annotation { "Feature Type Name" : "Feature", "Feature Type Description" : "" }
export const myFeature = defineFeature(function(context is Context, id is Id, definition is map)
    precondition{}
    {
        {
            var Q0;
            Q0=qCreatedBy(makeId("Top.planeOp"),FACE);
            var sketch = newSketch(context, id + "F0", { "sketchPlane" : qUnion([Q0])});
            skCircle(sketch, "E0", {"center": v(0, 0) * mm, "radius": 37.5 * mm});
            skSolve(sketch);
        }
        {
            var Q0;
            Q0 = qSketchRegion(id + "F0", true);
            extrude(context, id + "F1", {"entities" : qUnion([Q0]), "depth" : 6 * mm, "offsetDistance" : 25 * mm});
        }
        {
            var Q0;
            Q0=makeQuery(id+"F1.opExtrude","CAP_FACE",FACE,{"disambiguationData":[OSD([sQuery(id+"F0.wireOp",EDGE,"E0")])],"isStart":false});
            var sketch = newSketch(context, id + "F2", { "sketchPlane" : qUnion([Q0])});
            skCircle(sketch, "E1", {"center": v(0, 0) * mm, "radius": 36 * mm});
            skCircle(sketch, "E2.0", {"center": v(0, 0) * mm, "radius": 37.5 * mm});
            skSolve(sketch);
        }
        {
            var Q0;
            Q0 = qSketchRegion(id + "F2", true);
            extrude(context, id + "F3", {"entities" : qUnion([Q0]), "operationType" : NewBodyOperationType.ADD, "depth" : 12 * mm, "offsetDistance" : 25 * mm});
        }
        {
            var Q0;
            Q0=makeQuery(id+"F3.opExtrude","CAP_FACE",FACE,{"disambiguationData":[OSD([sQuery(id+"F2.wireOp",EDGE,"E1"),sQuery(id+"F2.wireOp",EDGE,"E2.0")])],"isStart":false});
            var sketch = newSketch(context, id + "F4", { "sketchPlane" : qUnion([Q0])});
            skArc(sketch, "E3", {"start": v(1.95, -37.45) * mm, "mid": v(2.76, -38.15) * mm, "end": v(3.45, -37.34) * mm});
            skArc(sketch, "E4.0", {"start": v(1.95, -37.45) * mm, "mid": v(2.7, -37.4) * mm, "end": v(3.45, -37.34) * mm});
            skSolve(sketch);
        }
        {
            var Q0;
            Q0=makeQuery(id+"F1.opExtrude","CAP_FACE",FACE,{"disambiguationData":[OSD([sQuery(id+"F0.wireOp",EDGE,"E0")])],"isStart":false});
            var sketch = newSketch(context, id + "F5", { "sketchPlane" : qUnion([Q0])});
            skCircle(sketch, "E5", {"center": v(0, 0) * mm, "radius": 32.75 * mm});
            skCircle(sketch, "E6", {"center": v(0, 0) * mm, "radius": 29.75 * mm});
            skSolve(sketch);
        }
        {
            var Q0;
            Q0 = qSketchRegion(id + "F5", true);
            extrude(context, id + "F6", {"entities" : qUnion([Q0]), "operationType" : NewBodyOperationType.ADD, "depth" : 10 * mm, "offsetDistance" : 25 * mm});
        }
        {
            var Q0;
            Q0=makeQuery(id+"F1.opExtrude","CAP_EDGE",EDGE,{"disambiguationData":[OSD([sQuery(id+"F0.wireOp",EDGE,"E0")])],"isStart":true});
            fillet(context, id + "F7", {"entities" : qUnion([Q0]), "radius" : 5 * mm, "tangentPropagation" : true, "allowEdgeOverflow" : false});
        }
        {
            var Q0;
            Q0=makeQuery(id+"F1.opExtrude","CAP_FACE",FACE,{"disambiguationData":[OSD([sQuery(id+"F0.wireOp",EDGE,"E0")])],"isStart":true});
            var sketch = newSketch(context, id + "F8", { "sketchPlane" : qUnion([Q0])});
            skText(sketch, "E7", { "text": "EXIN LIGHT", "fontName": "OpenSans-Bold.ttf"});
            const initialGuessF8  = {"E7": [-0.03112, -0.00426, 1, 0, 0.008]};
            skSetInitialGuess(sketch, initialGuessF8);
            skSolve(sketch);
        }
        {
            var Q0;
            Q0 = qSketchRegion(id + "F8", true);
            extrude(context, id + "F9", {"entities" : qUnion([Q0]), "operationType" : NewBodyOperationType.REMOVE, "oppositeDirection" : true, "depth" : 1 * mm, "offsetDistance" : 25 * mm});
        }
        {
            var Q0;
            Q0=makeQuery(id+"F1.opExtrude","CAP_FACE",FACE,{"disambiguationData":[OSD([sQuery(id+"F0.wireOp",EDGE,"E0")])],"isStart":true});
            chamfer(context, id + "F10", {"entities" : qUnion([Q0]), "width" : .4 * mm, "tangentPropagation" : true});
        }
        {
            var Q0;
            Q0=makeQuery(id+"F10.opChamfer","SPLIT",FACE,{"disambiguationData":[OD(1.0)],"derivedFrom":makeQuery(id+"F1.opExtrude","CAP_FACE",FACE,{"disambiguationData":[OSD([sQuery(id+"F0.wireOp",EDGE,"E0")])],"isStart":true})});
            var sketch = newSketch(context, id + "F11", { "sketchPlane" : qUnion([Q0])});
            skLineSegment(sketch, "E8.bottom", {"start": v(19.2, -26.22) * mm, "end": v(-19.2, -26.22) * mm});
            skLineSegment(sketch, "E8.top", {"start": v(14.23, -29.22) * mm, "end": v(-14.23, -29.22) * mm});
            skLineSegment(sketch, "E9.0.1.0", {"start": v(25.52, -20.12) * mm, "end": v(-25.52, -20.12) * mm});
            skLineSegment(sketch, "E9.0.1.1", {"start": v(22.84, -23.12) * mm, "end": v(-22.84, -23.12) * mm});
            skLineSegment(sketch, "E9.0.2.0", {"start": v(29.32, -14.02) * mm, "end": v(-29.32, -14.02) * mm});
            skLineSegment(sketch, "E9.0.2.1", {"start": v(27.69, -17.02) * mm, "end": v(-27.69, -17.02) * mm});
            skLineSegment(sketch, "E9.0.3.0", {"start": v(31.52, -7.92) * mm, "end": v(-31.52, -7.92) * mm});
            skLineSegment(sketch, "E9.0.3.1", {"start": v(30.61, -10.92) * mm, "end": v(-30.61, -10.92) * mm});
            skLineSegment(sketch, "E9.0.6.0", {"start": v(30.8, 10.38) * mm, "end": v(-30.8, 10.38) * mm});
            skLineSegment(sketch, "E9.0.6.1", {"start": v(31.65, 7.38) * mm, "end": v(-31.65, 7.38) * mm});
            skLineSegment(sketch, "E9.0.7.0", {"start": v(28.01, 16.48) * mm, "end": v(-28.01, 16.48) * mm});
            skLineSegment(sketch, "E9.0.7.1", {"start": v(29.57, 13.48) * mm, "end": v(-29.57, 13.48) * mm});
            skLineSegment(sketch, "E9.0.8.0", {"start": v(23.37, 22.58) * mm, "end": v(-23.37, 22.58) * mm});
            skLineSegment(sketch, "E9.0.8.1", {"start": v(25.94, 19.58) * mm, "end": v(-25.94, 19.58) * mm});
            skLineSegment(sketch, "E9.0.9.0", {"start": v(15.28, 28.68) * mm, "end": v(-15.28, 28.68) * mm});
            skLineSegment(sketch, "E9.0.9.1", {"start": v(19.92, 25.68) * mm, "end": v(-19.92, 25.68) * mm});
            skLineSegment(sketch, "E9.direction1", {"start": v(-14.23, -29.22) * mm, "end": v(-13.51, -29.22) * mm, "construction": true});
            skArc(sketch, "E10.0", {"start": v(-15.28, 28.68) * mm, "mid": v(-17.66, 27.28) * mm, "end": v(-19.92, 25.68) * mm});
            skPoint(sketch, "E11.orphan", {"position": v(41.49, -10.92) * mm});
            skPoint(sketch, "E12.orphan", {"position": v(41.49, -17.02) * mm});
            skPoint(sketch, "E13.orphan", {"position": v(41.49, -23.12) * mm});
            skPoint(sketch, "E14.orphan", {"position": v(41.49, -29.22) * mm});
            skPoint(sketch, "E15.orphan", {"position": v(41.49, 16.48) * mm});
            skPoint(sketch, "E16.orphan", {"position": v(41.49, 13.48) * mm});
            skArc(sketch, "E17.trimOffspring", {"start": v(19.92, 25.68) * mm, "mid": v(17.66, 27.28) * mm, "end": v(15.28, 28.68) * mm});
            skArc(sketch, "E18.trimOffspring", {"start": v(-23.37, 22.58) * mm, "mid": v(-24.7, 21.12) * mm, "end": v(-25.94, 19.58) * mm});
            skArc(sketch, "E19.trimOffspring", {"start": v(-28.01, 16.48) * mm, "mid": v(-28.83, 15) * mm, "end": v(-29.57, 13.48) * mm});
            skArc(sketch, "E20.trimOffspring", {"start": v(-30.8, 10.38) * mm, "mid": v(-31.26, 8.9) * mm, "end": v(-31.65, 7.38) * mm});
            skArc(sketch, "E21.trimOffspring", {"start": v(-31.52, -7.92) * mm, "mid": v(-31.1, -9.43) * mm, "end": v(-30.61, -10.92) * mm});
            skArc(sketch, "E22.trimOffspring", {"start": v(31.65, 7.38) * mm, "mid": v(31.26, 8.9) * mm, "end": v(30.8, 10.38) * mm});
            skArc(sketch, "E23.trimOffspring", {"start": v(29.57, 13.48) * mm, "mid": v(28.83, 15) * mm, "end": v(28.01, 16.48) * mm});
            skArc(sketch, "E24.trimOffspring", {"start": v(25.94, 19.58) * mm, "mid": v(24.7, 21.12) * mm, "end": v(23.37, 22.58) * mm});
            skArc(sketch, "E25.trimOffspring", {"start": v(30.61, -10.92) * mm, "mid": v(31.1, -9.43) * mm, "end": v(31.52, -7.92) * mm});
            skArc(sketch, "E26.trimOffspring", {"start": v(27.69, -17.02) * mm, "mid": v(28.54, -15.54) * mm, "end": v(29.32, -14.02) * mm});
            skArc(sketch, "E27.trimOffspring", {"start": v(22.84, -23.12) * mm, "mid": v(24.23, -21.66) * mm, "end": v(25.52, -20.12) * mm});
            skArc(sketch, "E28.trimOffspring", {"start": v(14.23, -29.22) * mm, "mid": v(16.79, -27.83) * mm, "end": v(19.2, -26.22) * mm});
            skArc(sketch, "E29.trimOffspring", {"start": v(-19.2, -26.22) * mm, "mid": v(-16.79, -27.83) * mm, "end": v(-14.23, -29.22) * mm});
            skArc(sketch, "E30.trimOffspring", {"start": v(-25.52, -20.12) * mm, "mid": v(-24.23, -21.66) * mm, "end": v(-22.84, -23.12) * mm});
            skArc(sketch, "E31.trimOffspring", {"start": v(-29.32, -14.02) * mm, "mid": v(-28.54, -15.54) * mm, "end": v(-27.69, -17.02) * mm});
            skSolve(sketch);
        }
        {
            var Q0;
            Q0 = qSketchRegion(id + "F11", true);
            extrude(context, id + "F12", {"entities" : qUnion([Q0]), "operationType" : NewBodyOperationType.REMOVE, "oppositeDirection" : true, "depth" : 5 * mm, "offsetDistance" : 25 * mm});
        }
    });